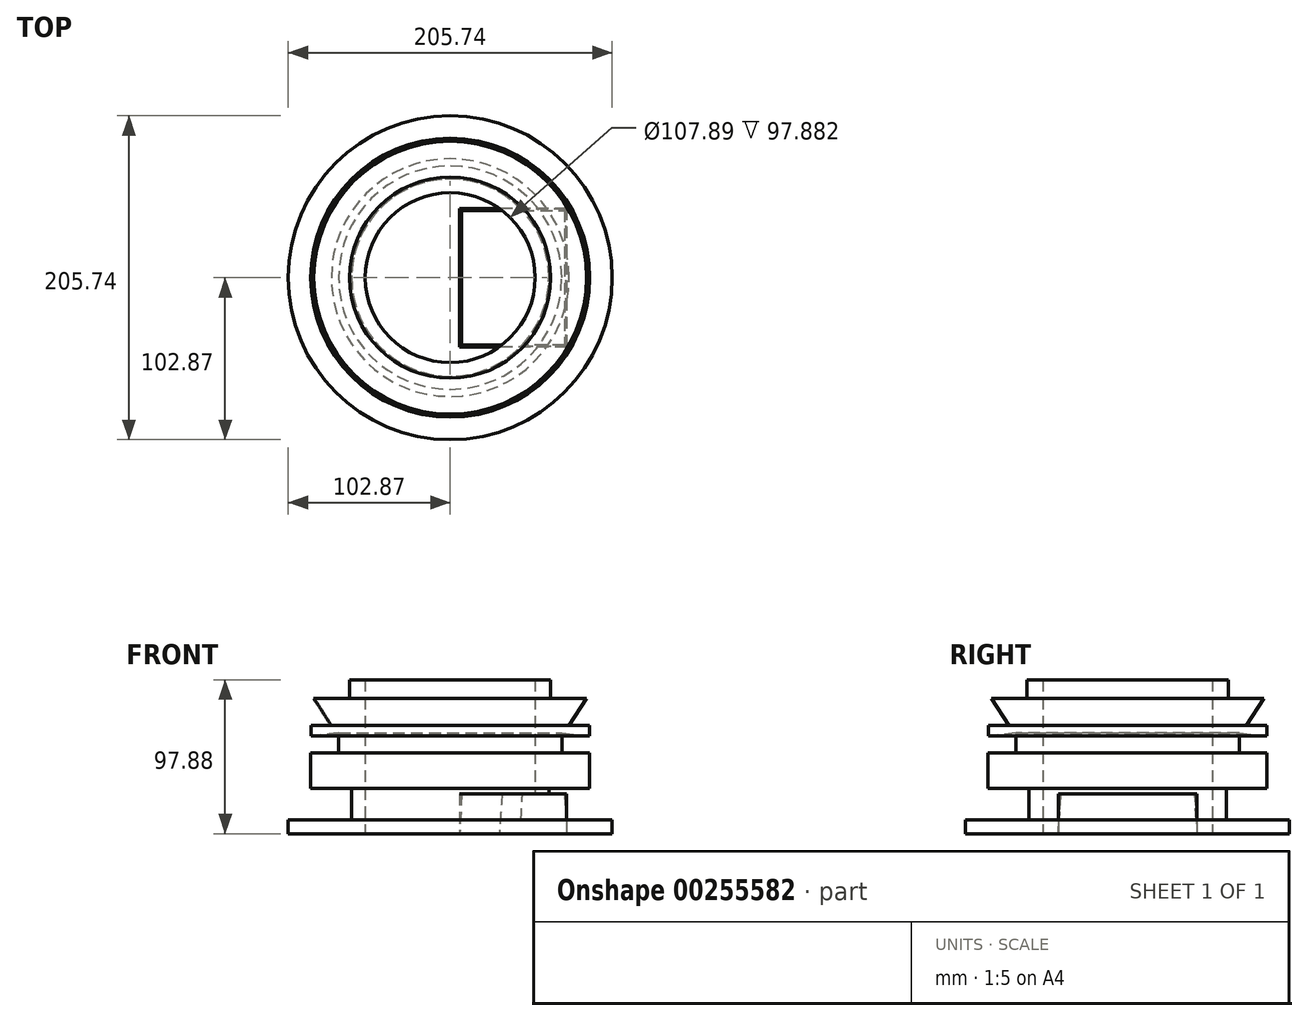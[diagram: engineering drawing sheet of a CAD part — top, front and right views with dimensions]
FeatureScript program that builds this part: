
annotation { "Feature Type Name" : "Feature", "Feature Type Description" : "" }
export const myFeature = defineFeature(function(context is Context, id is Id, definition is map)
    precondition{}
    {
        {
            var Q0;
            Q0=qCreatedBy(makeId("Top.planeOp"),FACE);
            var sketch = newSketch(context, id + "F0", { "sketchPlane" : qUnion([Q0])});
            skLineSegment(sketch, "E0.bottom", {"start": v(33.96, 44.03) * mm, "end": v(-33.96, 44.03) * mm});
            skLineSegment(sketch, "E0.top", {"start": v(33.96, -44.03) * mm, "end": v(-33.96, -44.03) * mm});
            skLineSegment(sketch, "E0.left", {"start": v(33.96, 44.03) * mm, "end": v(33.96, -44.03) * mm});
            skLineSegment(sketch, "E0.right", {"start": v(-33.96, 44.03) * mm, "end": v(-33.96, -44.03) * mm});
            skPoint(sketch, "E0.middle", {"position": v(0, 0) * mm});
            skSolve(sketch);
        }
        {
            var Q0;
            Q0=makeQuery(id+"F0.imprint","IMPRINT",FACE,{"disambiguationData":[TD([[makeQuery(id+"F0.imprint","IMPRINT",EDGE,{"derivedFrom":sQuery(id+"F0.wireOp",EDGE,"E0.bottom")}),1.0]])]});
            var Q1;
            Q1=sQuery(id+"F0.wireOp",EDGE,"E0.top");
            var Q2;
            Q2=sQuery(id+"F0.wireOp",EDGE,"E0.left");
            var Q3;
            Q3=sQuery(id+"F0.wireOp",EDGE,"E0.bottom");
            var Q4;
            Q4=sQuery(id+"F0.wireOp",EDGE,"E0.right");
            extrude(context, id + "F1", {"entities" : qUnion([Q0]), "surfaceEntities" : qUnion([Q1, Q2, Q3, Q4]), "depth" : 25.4 * mm, "hasDraft" : true, "draftAngle" : 3 * degree, "draftPullDirection" : true});
        }
        {
            var Q0;
            Q0=qCreatedBy(makeId("Front.planeOp"),FACE);
            var sketch = newSketch(context, id + "F2", { "sketchPlane" : qUnion([Q0])});
            skLineSegment(sketch, "E1", {"start": v(-40, 0) * mm, "end": v(-40, 76.5) * mm, "construction": true});
            skLineSegment(sketch, "E2", {"start": v(13.94, 0) * mm, "end": v(13.94, 97.88) * mm});
            skLineSegment(sketch, "E3", {"start": v(13.94, 97.88) * mm, "end": v(23.87, 97.88) * mm});
            skLineSegment(sketch, "E4", {"start": v(23.87, 97.88) * mm, "end": v(23.87, 86.01) * mm});
            skLineSegment(sketch, "E5", {"start": v(23.87, 86.01) * mm, "end": v(46.64, 86.01) * mm});
            skLineSegment(sketch, "E6", {"start": v(46.64, 86.01) * mm, "end": v(35.5, 68.82) * mm});
            skLineSegment(sketch, "E7", {"start": v(35.5, 68.82) * mm, "end": v(48.34, 68.82) * mm});
            skLineSegment(sketch, "E8", {"start": v(48.34, 68.82) * mm, "end": v(48.34, 62.04) * mm});
            skLineSegment(sketch, "E9", {"start": v(48.34, 62.04) * mm, "end": v(30.9, 63.97) * mm});
            skLineSegment(sketch, "E10", {"start": v(30.9, 63.97) * mm, "end": v(30.9, 51.38) * mm});
            skLineSegment(sketch, "E11", {"start": v(30.9, 51.38) * mm, "end": v(48.58, 51.38) * mm});
            skLineSegment(sketch, "E12", {"start": v(48.58, 51.38) * mm, "end": v(48.58, 28.85) * mm});
            skLineSegment(sketch, "E13", {"start": v(48.58, 28.85) * mm, "end": v(22.66, 28.85) * mm});
            skLineSegment(sketch, "E14", {"start": v(22.66, 28.85) * mm, "end": v(22.66, 8.75) * mm});
            skLineSegment(sketch, "E15", {"start": v(22.66, 8.75) * mm, "end": v(62.87, 8.75) * mm});
            skLineSegment(sketch, "E16", {"start": v(62.87, 8.75) * mm, "end": v(62.87, 0) * mm});
            skLineSegment(sketch, "E17", {"start": v(62.87, 0) * mm, "end": v(13.94, 0) * mm});
            skSolve(sketch);
        }
        {
            var Q0;
            Q0=makeQuery(id+"F2.imprint","IMPRINT",FACE,{"disambiguationData":[TD([[makeQuery(id+"F2.imprint","IMPRINT",EDGE,{"derivedFrom":sQuery(id+"F2.wireOp",EDGE,"E2")}),-1.0]])]});
            var Q1;
            Q1=sQuery(id+"F2.wireOp",EDGE,"E1");
            revolve(context, id + "F3", {"operationType" : NewBodyOperationType.ADD, "entities" : qUnion([Q0]), "axis" : qUnion([Q1]), "revolveType" : RevolveType.FULL});
        }
        {
            var Q0;
            Q0=makeQuery(id+"F0.imprint","IMPRINT",FACE,{"disambiguationData":[TD([[makeQuery(id+"F0.imprint","IMPRINT",EDGE,{"derivedFrom":sQuery(id+"F0.wireOp",EDGE,"E0.bottom")}),1.0]])]});
            extrude(context, id + "F4", {"entities" : qUnion([Q0]), "depth" : 25.4 * mm});
        }
    });
